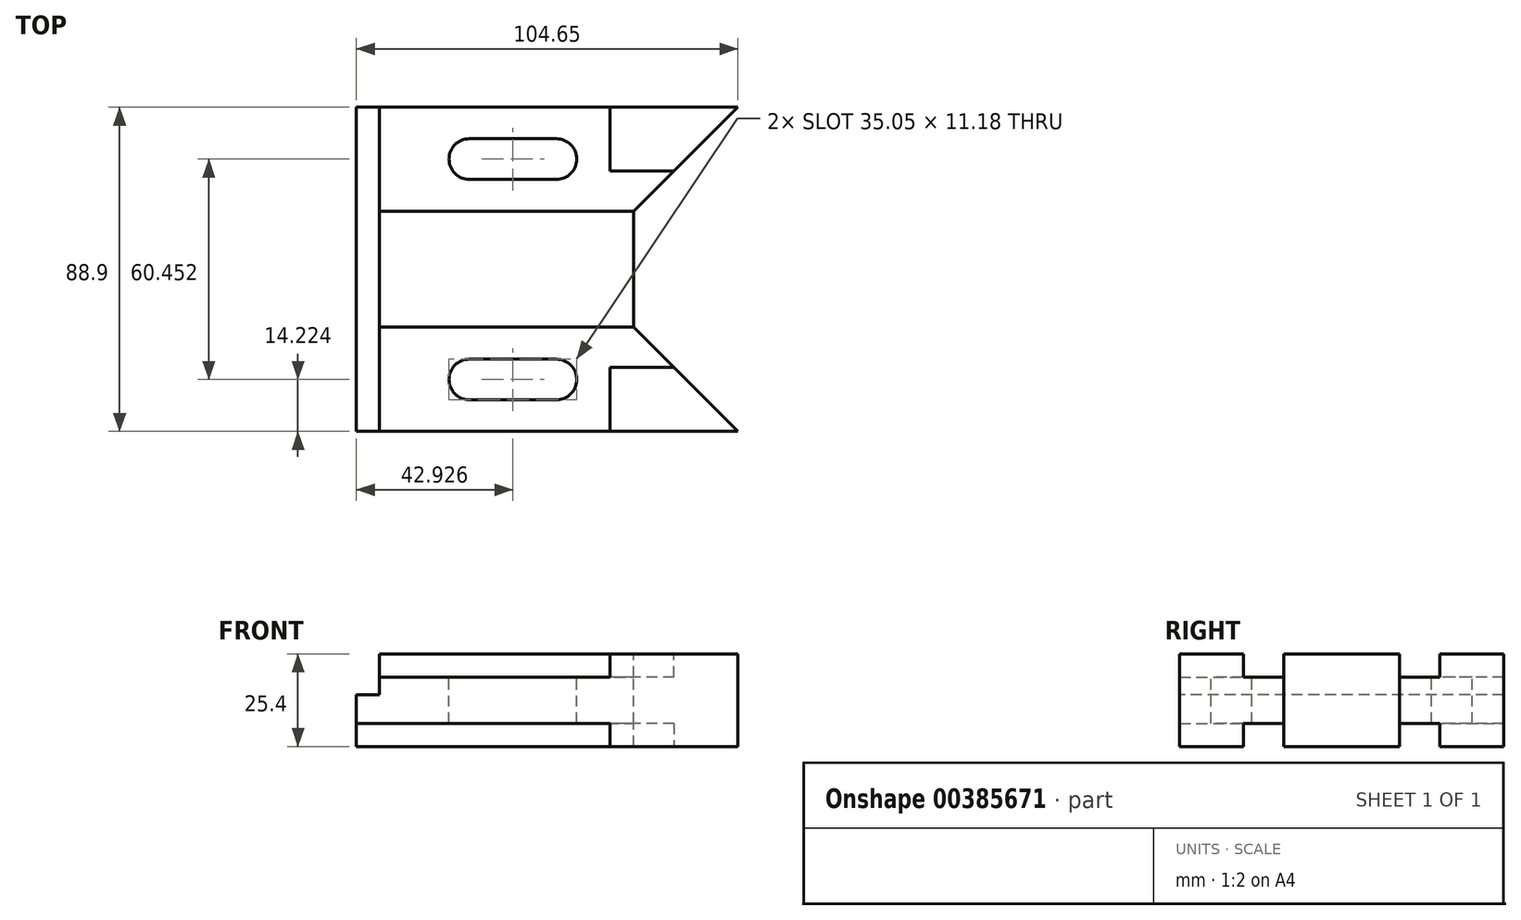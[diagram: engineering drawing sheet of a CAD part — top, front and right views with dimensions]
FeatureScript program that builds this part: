
annotation { "Feature Type Name" : "Feature", "Feature Type Description" : "" }
export const myFeature = defineFeature(function(context is Context, id is Id, definition is map)
    precondition{}
    {
        {
            var Q0;
            Q0=qCreatedBy(makeId("Top.planeOp"),FACE);
            var sketch = newSketch(context, id + "F0", { "sketchPlane" : qUnion([Q0])});
            skLineSegment(sketch, "E0", {"start": v(0, 0) * mm, "end": v(104.65, 0) * mm});
            skLineSegment(sketch, "E1", {"start": v(104.65, 0) * mm, "end": v(76.07, 28.58) * mm});
            skLineSegment(sketch, "E2", {"start": v(-12.2, 28.58) * mm, "end": v(148.43, 28.58) * mm, "construction": true});
            skLineSegment(sketch, "E3", {"start": v(-13.79, 44.45) * mm, "end": v(194.7, 44.45) * mm, "construction": true});
            skLineSegment(sketch, "E4.MirrorCS", {"start": v(0, 88.9) * mm, "end": v(104.65, 88.9) * mm});
            skLineSegment(sketch, "E5.MirrorCS", {"start": v(104.65, 88.9) * mm, "end": v(76.07, 60.33) * mm});
            skLineSegment(sketch, "E6", {"start": v(76.07, 28.58) * mm, "end": v(0, 28.58) * mm});
            skLineSegment(sketch, "E7", {"start": v(87.12, 17.53) * mm, "end": v(69.6, 17.53) * mm});
            skPoint(sketch, "E7.endSnap0", {"position": v(52.32, 0) * mm});
            skLineSegment(sketch, "E8", {"start": v(69.6, 0) * mm, "end": v(69.6, 17.53) * mm});
            skPoint(sketch, "E9.orphan", {"position": v(52.32, 17.53) * mm});
            skLineSegment(sketch, "E10", {"start": v(6.35, 0) * mm, "end": v(6.35, 28.58) * mm});
            skArc(sketch, "E11", {"start": v(30.99, 19.81) * mm, "mid": v(25.4, 14.22) * mm, "end": v(30.99, 8.64) * mm});
            skArc(sketch, "E12", {"start": v(54.86, 8.64) * mm, "mid": v(60.45, 14.22) * mm, "end": v(54.86, 19.81) * mm});
            skLineSegment(sketch, "E13", {"start": v(30.99, 8.64) * mm, "end": v(54.86, 8.64) * mm});
            skLineSegment(sketch, "E14", {"start": v(30.99, 19.81) * mm, "end": v(54.86, 19.81) * mm});
            skLineSegment(sketch, "E15.MirrorCS", {"start": v(87.12, 71.37) * mm, "end": v(69.6, 71.37) * mm});
            skLineSegment(sketch, "E16.MirrorCS", {"start": v(69.6, 88.9) * mm, "end": v(69.6, 71.37) * mm});
            skArc(sketch, "E17.MirrorCS", {"start": v(30.99, 69.09) * mm, "mid": v(25.4, 74.68) * mm, "end": v(30.99, 80.26) * mm});
            skLineSegment(sketch, "E18.MirrorCS", {"start": v(30.99, 69.09) * mm, "end": v(54.86, 69.09) * mm});
            skArc(sketch, "E19.MirrorCS", {"start": v(54.86, 80.26) * mm, "mid": v(60.45, 74.68) * mm, "end": v(54.86, 69.09) * mm});
            skLineSegment(sketch, "E20.MirrorCS", {"start": v(30.99, 80.26) * mm, "end": v(54.86, 80.26) * mm});
            skLineSegment(sketch, "E21.MirrorCS", {"start": v(6.35, 88.9) * mm, "end": v(6.35, 60.32) * mm});
            skLineSegment(sketch, "E22", {"start": v(6.35, 60.33) * mm, "end": v(76.07, 60.33) * mm});
            skLineSegment(sketch, "E23", {"start": v(0, 88.9) * mm, "end": v(0, 0) * mm});
            skLineSegment(sketch, "E24", {"start": v(6.35, 60.33) * mm, "end": v(6.35, 28.58) * mm});
            skLineSegment(sketch, "E25", {"start": v(76.07, 60.33) * mm, "end": v(76.07, 28.58) * mm});
            skLineSegment(sketch, "E26", {"start": v(6.35, 60.33) * mm, "end": v(0, 60.33) * mm});
            skSolve(sketch);
        }
        {
            var Q0;
            Q0 = qSketchRegion(id + "F0", true);
            extrude(context, id + "F1", {"entities" : qUnion([Q0]), "oppositeDirection" : true, "depth" : 25.4 * mm});
        }
        {
            var Q0;
            {var subQ0=sQuery(id+"F0.wireOp",EDGE,"E7");Q0=makeQuery(id+"F0.imprint","IMPRINT",FACE,{"disambiguationData":[TD([[makeQuery(id+"F0.imprint","IMPRINT",EDGE,{"derivedFrom":subQ0}),-1.0]])]});}
            extrude(context, id + "F2", {"entities" : qUnion([Q0]), "operationType" : NewBodyOperationType.REMOVE, "oppositeDirection" : true, "depth" : 6.35 * mm});
        }
        {
            var Q0;
            {var subQ3=sQuery(id+"F0.wireOp",EDGE,"E15.MirrorCS");Q0=makeQuery(id+"F0.imprint","IMPRINT",FACE,{"disambiguationData":[TD([[makeQuery(id+"F0.imprint","IMPRINT",EDGE,{"derivedFrom":subQ3}),1.0]])]});}
            extrude(context, id + "F3", {"entities" : qUnion([Q0]), "operationType" : NewBodyOperationType.REMOVE, "oppositeDirection" : true, "depth" : 6.35 * mm});
        }
        {
            var Q0;
            {var subQ3=sQuery(id+"F0.wireOp",EDGE,"E10");Q0=makeQuery(id+"F0.imprint","IMPRINT",FACE,{"disambiguationData":[TD([[makeQuery(id+"F0.imprint","IMPRINT",EDGE,{"derivedFrom":subQ3}),1.0]])]});}
            var Q1;
            {var subQ3=sQuery(id+"F0.wireOp",EDGE,"E24");Q1=makeQuery(id+"F0.imprint","IMPRINT",FACE,{"disambiguationData":[TD([[makeQuery(id+"F0.imprint","IMPRINT",EDGE,{"derivedFrom":subQ3}),-1.0]])]});}
            var Q2;
            {var subQ3=sQuery(id+"F0.wireOp",EDGE,"E21.MirrorCS");Q2=makeQuery(id+"F0.imprint","IMPRINT",FACE,{"disambiguationData":[TD([[makeQuery(id+"F0.imprint","IMPRINT",EDGE,{"derivedFrom":subQ3}),-1.0]])]});}
            extrude(context, id + "F4", {"entities" : qUnion([Q0, Q1, Q2]), "operationType" : NewBodyOperationType.REMOVE, "oppositeDirection" : true, "depth" : 11.18 * mm});
        }
        {
            var Q0;
            Q0=qCreatedBy(makeId("Top.planeOp"),FACE);
            cPlane(context, id + "F5", {"entities" : qUnion([Q0]), "cplaneType" : CPlaneType.OFFSET, "offset" : 25.4 * mm, "oppositeDirection" : true, "width" : 152.4 * mm, "height" : 152.4 * mm});
        }
        {
            var Q0;
            Q0=qCreatedBy(id+"F5.planeOp",FACE);
            var sketch = newSketch(context, id + "F6", { "sketchPlane" : qUnion([Q0])});
            skLineSegment(sketch, "E27.0", {"start": v(0, 0) * mm, "end": v(69.6, 0) * mm});
            skPoint(sketch, "E28.0", {"position": v(69.6, 8.76) * mm});
            skPoint(sketch, "E29.0", {"position": v(78.36, 17.53) * mm});
            skLineSegment(sketch, "E30.0", {"start": v(76.07, 28.58) * mm, "end": v(0, 28.58) * mm});
            skLineSegment(sketch, "E31.0", {"start": v(0, 60.32) * mm, "end": v(76.07, 60.33) * mm});
            skPoint(sketch, "E32.0", {"position": v(78.36, 71.37) * mm});
            skPoint(sketch, "E33.0", {"position": v(69.6, 80.14) * mm});
            skLineSegment(sketch, "E34.0", {"start": v(0, 88.9) * mm, "end": v(69.6, 88.9) * mm});
            skPoint(sketch, "E35.orphan", {"position": v(6.35, 60.33) * mm});
            skLineSegment(sketch, "E36.0", {"start": v(69.6, 0) * mm, "end": v(69.6, 17.53) * mm});
            skLineSegment(sketch, "E37.0", {"start": v(87.12, 17.53) * mm, "end": v(69.6, 17.53) * mm});
            skLineSegment(sketch, "E38.0", {"start": v(87.12, 71.37) * mm, "end": v(69.6, 71.37) * mm});
            skLineSegment(sketch, "E39.0", {"start": v(69.6, 88.9) * mm, "end": v(69.6, 71.37) * mm});
            skLineSegment(sketch, "E40.0", {"start": v(87.12, 17.53) * mm, "end": v(76.07, 28.58) * mm});
            skLineSegment(sketch, "E41.0", {"start": v(87.12, 71.37) * mm, "end": v(76.07, 60.33) * mm});
            skPoint(sketch, "E42.orphan", {"position": v(104.65, 0) * mm});
            skPoint(sketch, "E43.orphan", {"position": v(104.65, 88.9) * mm});
            skLineSegment(sketch, "E44", {"start": v(0, 0) * mm, "end": v(0, 28.58) * mm});
            skLineSegment(sketch, "E45", {"start": v(0, 60.32) * mm, "end": v(0, 88.9) * mm});
            skSolve(sketch);
        }
        {
            var Q0;
            Q0=makeQuery(id+"F6.imprint","IMPRINT",FACE,{"disambiguationData":[TD([[makeQuery(id+"F6.imprint","IMPRINT",EDGE,{"derivedFrom":sQuery(id+"F6.wireOp",EDGE,"E27.0")}),1.0]])]});
            var Q1;
            Q1=makeQuery(id+"F6.imprint","IMPRINT",FACE,{"disambiguationData":[TD([[makeQuery(id+"F6.imprint","IMPRINT",EDGE,{"derivedFrom":sQuery(id+"F6.wireOp",EDGE,"E31.0")}),1.0]])]});
            extrude(context, id + "F7", {"entities" : qUnion([Q0, Q1]), "operationType" : NewBodyOperationType.REMOVE, "depth" : 6.35 * mm});
        }
    });
